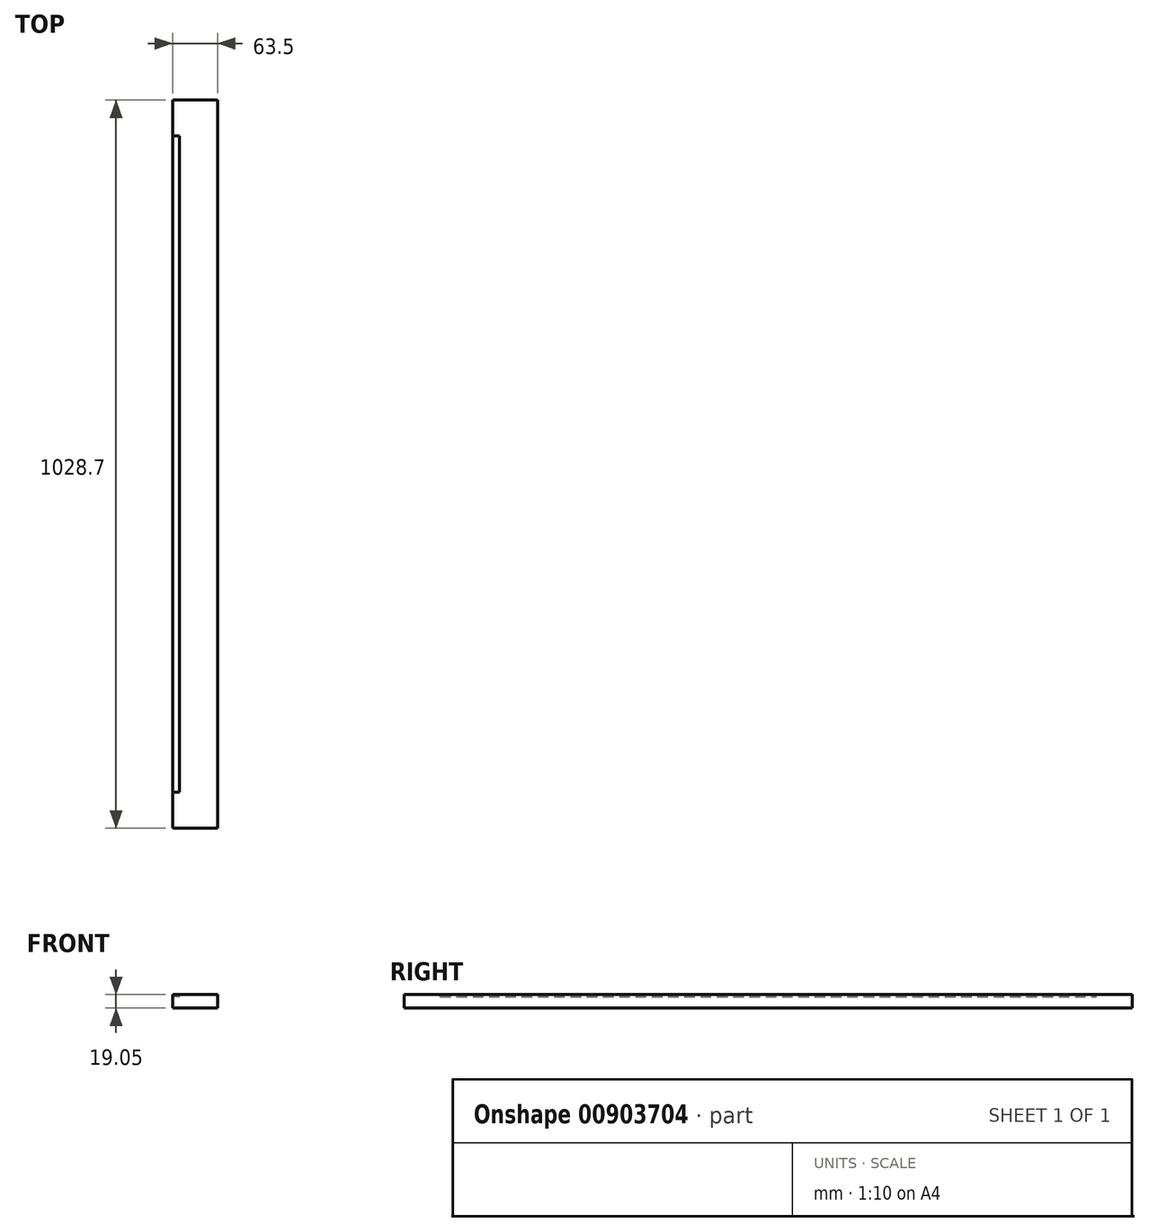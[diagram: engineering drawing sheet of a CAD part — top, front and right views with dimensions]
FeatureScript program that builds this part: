
annotation { "Feature Type Name" : "Feature", "Feature Type Description" : "" }
export const myFeature = defineFeature(function(context is Context, id is Id, definition is map)
    precondition{}
    {
        {
            var Q0;
            Q0=qCreatedBy(makeId("Top.planeOp"),FACE);
            var sketch = newSketch(context, id + "F0", { "sketchPlane" : qUnion([Q0])});
            skLineSegment(sketch, "E0.bottom", {"start": v(0, -514.35) * mm, "end": v(-63.5, -514.35) * mm});
            skLineSegment(sketch, "E0.top", {"start": v(0, 514.35) * mm, "end": v(-63.5, 514.35) * mm});
            skLineSegment(sketch, "E0.left", {"start": v(0, -514.35) * mm, "end": v(0, 514.35) * mm});
            skLineSegment(sketch, "E0.right", {"start": v(-63.5, -514.35) * mm, "end": v(-63.5, 514.35) * mm});
            skSolve(sketch);
        }
        {
            var Q0;
            Q0=makeQuery(id+"F0.imprint","IMPRINT",FACE,{"disambiguationData":[TD([[makeQuery(id+"F0.imprint","IMPRINT",EDGE,{"derivedFrom":sQuery(id+"F0.wireOp",EDGE,"E0.bottom")}),-1.0]])]});
            extrude(context, id + "F1", {"entities" : qUnion([Q0]), "depth" : 19.05 * mm, "offsetDistance" : 25 * mm});
        }
        {
            var Q0;
            Q0=qCreatedBy(makeId("Front.planeOp"),FACE);
            var sketch = newSketch(context, id + "F2", { "sketchPlane" : qUnion([Q0])});
            skLineSegment(sketch, "E1.bottom", {"start": v(-53.98, 15.88) * mm, "end": v(-63.5, 15.88) * mm});
            skLineSegment(sketch, "E1.top", {"start": v(-53.98, 19.05) * mm, "end": v(-63.5, 19.05) * mm});
            skLineSegment(sketch, "E1.left", {"start": v(-53.98, 15.88) * mm, "end": v(-53.98, 19.05) * mm});
            skLineSegment(sketch, "E1.right", {"start": v(-63.5, 15.88) * mm, "end": v(-63.5, 19.05) * mm});
            skSolve(sketch);
        }
        {
            var Q0;
            Q0 = qSketchRegion(id + "F2", true);
            extrude(context, id + "F3", {"entities" : qUnion([Q0]), "operationType" : NewBodyOperationType.REMOVE, "depth" : 463.55 * mm, "offsetDistance" : 25.4 * mm, "hasSecondDirection" : true, "secondDirectionOppositeDirection" : true, "secondDirectionDepth" : 463.55 * mm});
        }
    });
